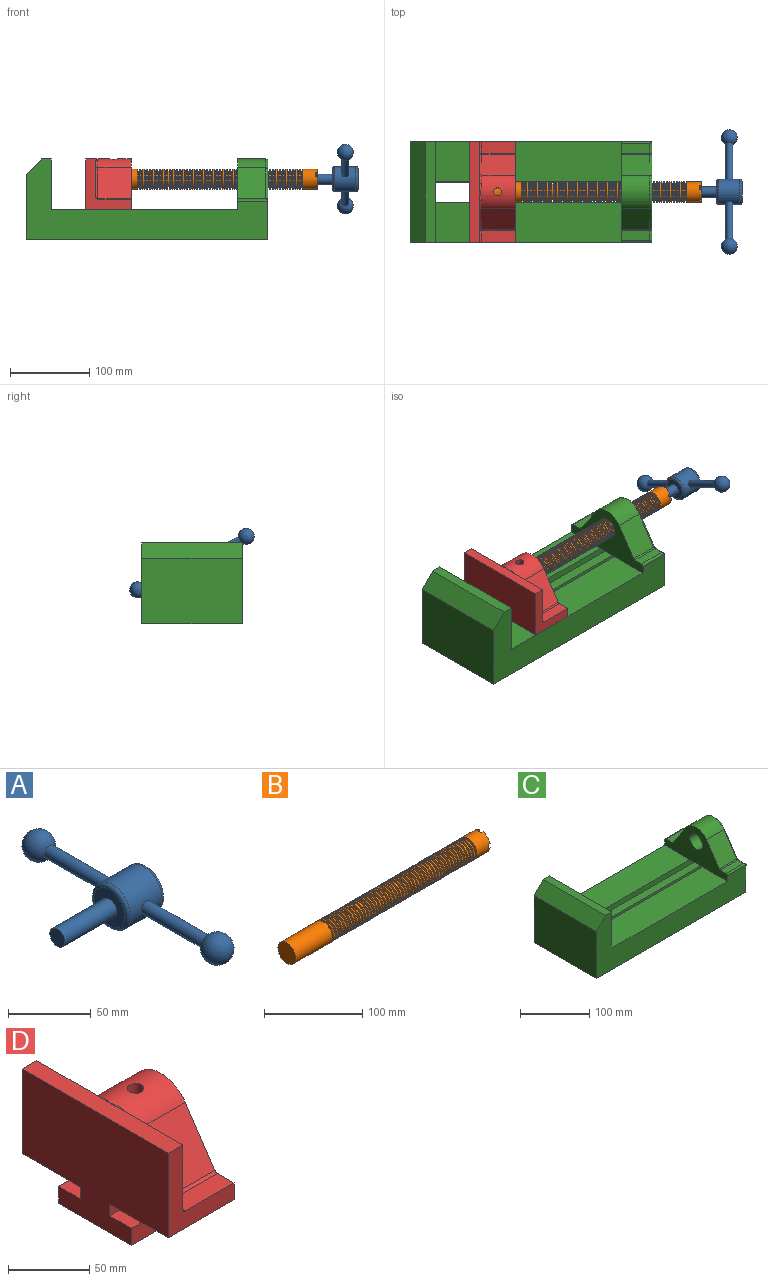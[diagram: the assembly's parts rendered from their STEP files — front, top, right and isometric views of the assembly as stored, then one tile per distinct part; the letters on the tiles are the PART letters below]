
ASSEMBLY  parts=4 mates=3
PART A: 11 faces, bbox 76.2x172.7x34.4 mm
  f0: sphere r=10.16mm, area 1231.8mm2, adj f1
  f1: cylinder r=4.45mm len=51.82mm, axis (0,1,0), area 1438.5mm2, adj f0,f4
  f2: sphere r=10.16mm, area 1231.8mm2, adj f3
  f3: cylinder r=4.45mm len=51.82mm, axis (0,1,0), area 1438.5mm2, adj f2,f4
  f4: cylinder r=15.88mm len=31.75mm, axis (-1,0,0), area 2534.7mm2, adj f1,f3,f9,f10
  f5: cylinder r=6.35mm len=44.45mm, axis (-1,0,0), area 1773.5mm2, adj f6,f8
  f6: plane 12.7x12.7mm, normal (-1,0,0), area 126.7mm2, adj f5
  f7: plane 26.67x26.67mm, normal (1,0,0), area 558.6mm2, adj f10
  f8: plane 26.67x26.67mm, normal (-1,0,0), area 432mm2, adj f5,f9
  f9: torus R=13.33mm, axis (1,0,0), area 374.8mm2, adj f4,f8
  f10: torus R=13.33mm, axis (1,0,0), area 374.8mm2, adj f4,f7
PART B: 220 faces, bbox 279.4x25.4x25.4 mm
  f0: cylinder r=12.7mm len=25.4mm, axis (-1,0,0), area 1468.2mm2, adj f1,f2,f3,f5,f7,f208,f209,f210
  f1: plane 9.9x9.9mm, normal (1,0,0), area 62.3mm2, adj f0,f4,f213,f216
  f2: plane 9.9x9.9mm, normal (1,0,0), area 62.3mm2, adj f0,f4,f210,f218
  f3: plane 9.9x9.9mm, normal (1,0,0), area 62.3mm2, adj f0,f4,f209,f212
  f4: cylinder r=6.35mm len=25.4mm, axis (1,0,0), area 960.3mm2, adj f1,f2,f3,f5,f6,f208,f209,f210
  f5: plane 9.9x9.9mm, normal (1,0,0), area 62.3mm2, adj f0,f4,f215,f217
  f6: plane 12.7x12.7mm, normal (1,0,0), area 126.7mm2, adj f4
  f7: cone r=12.7mm half-angle=76deg, axis (1,0,0), area 188mm2, adj f0,f9
  f8: cone r=10.16mm half-angle=76deg, axis (-1,0,0), area 188mm2, adj f9,f10
  f9: cylinder r=10.16mm len=20.32mm, axis (1,0,0), area 81.1mm2, adj f7,f8
  f10: cylinder r=12.7mm len=25.4mm, axis (-1,0,0), area 131.7mm2, adj f8,f11
  f11: cone r=12.7mm half-angle=76deg, axis (1,0,0), area 188mm2, adj f10,f13
  f12: cone r=10.16mm half-angle=76deg, axis (-1,0,0), area 188mm2, adj f13,f14
  f13: cylinder r=10.16mm len=20.32mm, axis (1,0,0), area 81.1mm2, adj f11,f12
  f14: cylinder r=12.7mm len=25.4mm, axis (-1,0,0), area 131.7mm2, adj f12,f15
  f15: cone r=12.7mm half-angle=76deg, axis (1,0,0), area 188mm2, adj f14,f17
  f16: cone r=10.16mm half-angle=76deg, axis (-1,0,0), area 188mm2, adj f17,f18
  f17: cylinder r=10.16mm len=20.32mm, axis (1,0,0), area 81.1mm2, adj f15,f16
  f18: cylinder r=12.7mm len=25.4mm, axis (-1,0,0), area 131.7mm2, adj f16,f19
  f19: cone r=12.7mm half-angle=76deg, axis (1,0,0), area 188mm2, adj f18,f21
  f20: cone r=10.16mm half-angle=76deg, axis (-1,0,0), area 188mm2, adj f21,f22
  f21: cylinder r=10.16mm len=20.32mm, axis (1,0,0), area 81.1mm2, adj f19,f20
  f22: cylinder r=12.7mm len=25.4mm, axis (-1,0,0), area 131.7mm2, adj f20,f23
  f23: cone r=12.7mm half-angle=76deg, axis (1,0,0), area 188mm2, adj f22,f25
  f24: cone r=10.16mm half-angle=76deg, axis (-1,0,0), area 188mm2, adj f25,f26
  f25: cylinder r=10.16mm len=20.32mm, axis (1,0,0), area 81.1mm2, adj f23,f24
  f26: cylinder r=12.7mm len=25.4mm, axis (-1,0,0), area 131.7mm2, adj f24,f27
  f27: cone r=12.7mm half-angle=76deg, axis (1,0,0), area 188mm2, adj f26,f29
  f28: cone r=10.16mm half-angle=76deg, axis (-1,0,0), area 188mm2, adj f29,f30
  f29: cylinder r=10.16mm len=20.32mm, axis (1,0,0), area 81.1mm2, adj f27,f28
  f30: cylinder r=12.7mm len=25.4mm, axis (-1,0,0), area 131.7mm2, adj f28,f31
  f31: cone r=12.7mm half-angle=76deg, axis (1,0,0), area 188mm2, adj f30,f33
  f32: cone r=10.16mm half-angle=76deg, axis (-1,0,0), area 188mm2, adj f33,f34
  f33: cylinder r=10.16mm len=20.32mm, axis (1,0,0), area 81.1mm2, adj f31,f32
  f34: cylinder r=12.7mm len=25.4mm, axis (-1,0,0), area 131.7mm2, adj f32,f35
  f35: cone r=12.7mm half-angle=76deg, axis (1,0,0), area 188mm2, adj f34,f37
  f36: cone r=10.16mm half-angle=76deg, axis (-1,0,0), area 188mm2, adj f37,f38
  f37: cylinder r=10.16mm len=20.32mm, axis (1,0,0), area 81.1mm2, adj f35,f36
  f38: cylinder r=12.7mm len=25.4mm, axis (-1,0,0), area 131.7mm2, adj f36,f39
  f39: cone r=12.7mm half-angle=76deg, axis (1,0,0), area 188mm2, adj f38,f41
  f40: cone r=10.16mm half-angle=76deg, axis (-1,0,0), area 188mm2, adj f41,f42
  f41: cylinder r=10.16mm len=20.32mm, axis (1,0,0), area 81.1mm2, adj f39,f40
  f42: cylinder r=12.7mm len=25.4mm, axis (-1,0,0), area 131.7mm2, adj f40,f43
  f43: cone r=12.7mm half-angle=76deg, axis (1,0,0), area 188mm2, adj f42,f45
  f44: cone r=10.16mm half-angle=76deg, axis (-1,0,0), area 188mm2, adj f45,f46
  f45: cylinder r=10.16mm len=20.32mm, axis (1,0,0), area 81.1mm2, adj f43,f44
  f46: cylinder r=12.7mm len=25.4mm, axis (-1,0,0), area 131.7mm2, adj f44,f47
  f47: cone r=12.7mm half-angle=76deg, axis (1,0,0), area 188mm2, adj f46,f49
  f48: cone r=10.16mm half-angle=76deg, axis (-1,0,0), area 188mm2, adj f49,f50
  f49: cylinder r=10.16mm len=20.32mm, axis (1,0,0), area 81.1mm2, adj f47,f48
  f50: cylinder r=12.7mm len=25.4mm, axis (-1,0,0), area 131.7mm2, adj f48,f51
  f51: cone r=12.7mm half-angle=76deg, axis (1,0,0), area 188mm2, adj f50,f53
  f52: cone r=10.16mm half-angle=76deg, axis (-1,0,0), area 188mm2, adj f53,f54
  f53: cylinder r=10.16mm len=20.32mm, axis (1,0,0), area 81.1mm2, adj f51,f52
  f54: cylinder r=12.7mm len=25.4mm, axis (-1,0,0), area 131.7mm2, adj f52,f55
  f55: cone r=12.7mm half-angle=76deg, axis (1,0,0), area 188mm2, adj f54,f57
  f56: cone r=10.16mm half-angle=76deg, axis (-1,0,0), area 188mm2, adj f57,f58
  f57: cylinder r=10.16mm len=20.32mm, axis (1,0,0), area 81.1mm2, adj f55,f56
  f58: cylinder r=12.7mm len=25.4mm, axis (-1,0,0), area 131.7mm2, adj f56,f59
  f59: cone r=12.7mm half-angle=76deg, axis (1,0,0), area 188mm2, adj f58,f61
  f60: cone r=10.16mm half-angle=76deg, axis (-1,0,0), area 188mm2, adj f61,f62
  f61: cylinder r=10.16mm len=20.32mm, axis (1,0,0), area 81.1mm2, adj f59,f60
  f62: cylinder r=12.7mm len=25.4mm, axis (-1,0,0), area 131.7mm2, adj f60,f63
  f63: cone r=12.7mm half-angle=76deg, axis (1,0,0), area 188mm2, adj f62,f65
  f64: cone r=10.16mm half-angle=76deg, axis (-1,0,0), area 188mm2, adj f65,f66
  f65: cylinder r=10.16mm len=20.32mm, axis (1,0,0), area 81.1mm2, adj f63,f64
  f66: cylinder r=12.7mm len=25.4mm, axis (-1,0,0), area 131.7mm2, adj f64,f67
  f67: cone r=12.7mm half-angle=76deg, axis (1,0,0), area 188mm2, adj f66,f69
  f68: cone r=10.16mm half-angle=76deg, axis (-1,0,0), area 188mm2, adj f69,f70
  f69: cylinder r=10.16mm len=20.32mm, axis (1,0,0), area 81.1mm2, adj f67,f68
  f70: cylinder r=12.7mm len=25.4mm, axis (-1,0,0), area 131.7mm2, adj f68,f71
  f71: cone r=12.7mm half-angle=76deg, axis (1,0,0), area 188mm2, adj f70,f73
  f72: cone r=10.16mm half-angle=76deg, axis (-1,0,0), area 188mm2, adj f73,f74
  f73: cylinder r=10.16mm len=20.32mm, axis (1,0,0), area 81.1mm2, adj f71,f72
  f74: cylinder r=12.7mm len=25.4mm, axis (-1,0,0), area 131.7mm2, adj f72,f75
  f75: cone r=12.7mm half-angle=76deg, axis (1,0,0), area 188mm2, adj f74,f77
  f76: cone r=10.16mm half-angle=76deg, axis (-1,0,0), area 188mm2, adj f77,f78
  f77: cylinder r=10.16mm len=20.32mm, axis (1,0,0), area 81.1mm2, adj f75,f76
  f78: cylinder r=12.7mm len=25.4mm, axis (-1,0,0), area 131.7mm2, adj f76,f79
  f79: cone r=12.7mm half-angle=76deg, axis (1,0,0), area 188mm2, adj f78,f81
  f80: cone r=10.16mm half-angle=76deg, axis (-1,0,0), area 188mm2, adj f81,f82
  f81: cylinder r=10.16mm len=20.32mm, axis (1,0,0), area 81.1mm2, adj f79,f80
  f82: cylinder r=12.7mm len=25.4mm, axis (-1,0,0), area 131.7mm2, adj f80,f83
  f83: cone r=12.7mm half-angle=76deg, axis (1,0,0), area 188mm2, adj f82,f85
  f84: cone r=10.16mm half-angle=76deg, axis (-1,0,0), area 188mm2, adj f85,f86
  f85: cylinder r=10.16mm len=20.32mm, axis (1,0,0), area 81.1mm2, adj f83,f84
  f86: cylinder r=12.7mm len=25.4mm, axis (-1,0,0), area 131.7mm2, adj f84,f87
  f87: cone r=12.7mm half-angle=76deg, axis (1,0,0), area 188mm2, adj f86,f89
  f88: cone r=10.16mm half-angle=76deg, axis (-1,0,0), area 188mm2, adj f89,f90
  f89: cylinder r=10.16mm len=20.32mm, axis (1,0,0), area 81.1mm2, adj f87,f88
  f90: cylinder r=12.7mm len=25.4mm, axis (-1,0,0), area 131.7mm2, adj f88,f91
  f91: cone r=12.7mm half-angle=76deg, axis (1,0,0), area 188mm2, adj f90,f93
  f92: cone r=10.16mm half-angle=76deg, axis (-1,0,0), area 188mm2, adj f93,f94
  f93: cylinder r=10.16mm len=20.32mm, axis (1,0,0), area 81.1mm2, adj f91,f92
  f94: cylinder r=12.7mm len=25.4mm, axis (-1,0,0), area 131.7mm2, adj f92,f95
  f95: cone r=12.7mm half-angle=76deg, axis (1,0,0), area 188mm2, adj f94,f97
  f96: cone r=10.16mm half-angle=76deg, axis (-1,0,0), area 188mm2, adj f97,f98
  f97: cylinder r=10.16mm len=20.32mm, axis (1,0,0), area 81.1mm2, adj f95,f96
  f98: cylinder r=12.7mm len=25.4mm, axis (-1,0,0), area 131.7mm2, adj f96,f99
  f99: cone r=12.7mm half-angle=76deg, axis (1,0,0), area 188mm2, adj f98,f101
  f100: cone r=10.16mm half-angle=76deg, axis (-1,0,0), area 188mm2, adj f101,f102
  f101: cylinder r=10.16mm len=20.32mm, axis (1,0,0), area 81.1mm2, adj f99,f100
  f102: cylinder r=12.7mm len=25.4mm, axis (-1,0,0), area 131.7mm2, adj f100,f103
  f103: cone r=12.7mm half-angle=76deg, axis (1,0,0), area 188mm2, adj f102,f105
  f104: cone r=10.16mm half-angle=76deg, axis (-1,0,0), area 188mm2, adj f105,f106
  f105: cylinder r=10.16mm len=20.32mm, axis (1,0,0), area 81.1mm2, adj f103,f104
  f106: cylinder r=12.7mm len=25.4mm, axis (-1,0,0), area 131.7mm2, adj f104,f107
  f107: cone r=12.7mm half-angle=76deg, axis (1,0,0), area 188mm2, adj f106,f109
  f108: cone r=10.16mm half-angle=76deg, axis (-1,0,0), area 188mm2, adj f109,f110
  f109: cylinder r=10.16mm len=20.32mm, axis (1,0,0), area 81.1mm2, adj f107,f108
  f110: cylinder r=12.7mm len=25.4mm, axis (-1,0,0), area 131.7mm2, adj f108,f111
  f111: cone r=12.7mm half-angle=76deg, axis (1,0,0), area 188mm2, adj f110,f113
  f112: cone r=10.16mm half-angle=76deg, axis (-1,0,0), area 188mm2, adj f113,f114
  f113: cylinder r=10.16mm len=20.32mm, axis (1,0,0), area 81.1mm2, adj f111,f112
  f114: cylinder r=12.7mm len=25.4mm, axis (-1,0,0), area 131.7mm2, adj f112,f115
  f115: cone r=12.7mm half-angle=76deg, axis (1,0,0), area 188mm2, adj f114,f117
  f116: cone r=10.16mm half-angle=76deg, axis (-1,0,0), area 188mm2, adj f117,f118
  f117: cylinder r=10.16mm len=20.32mm, axis (1,0,0), area 81.1mm2, adj f115,f116
  f118: cylinder r=12.7mm len=25.4mm, axis (-1,0,0), area 131.7mm2, adj f116,f119
  f119: cone r=12.7mm half-angle=76deg, axis (1,0,0), area 188mm2, adj f118,f121
  f120: cone r=10.16mm half-angle=76deg, axis (-1,0,0), area 188mm2, adj f121,f122
  f121: cylinder r=10.16mm len=20.32mm, axis (1,0,0), area 81.1mm2, adj f119,f120
  f122: cylinder r=12.7mm len=25.4mm, axis (-1,0,0), area 131.7mm2, adj f120,f123
  f123: cone r=12.7mm half-angle=76deg, axis (1,0,0), area 188mm2, adj f122,f125
  f124: cone r=10.16mm half-angle=76deg, axis (-1,0,0), area 188mm2, adj f125,f126
  f125: cylinder r=10.16mm len=20.32mm, axis (1,0,0), area 81.1mm2, adj f123,f124
  f126: cylinder r=12.7mm len=25.4mm, axis (-1,0,0), area 131.7mm2, adj f124,f127
  f127: cone r=12.7mm half-angle=76deg, axis (1,0,0), area 188mm2, adj f126,f129
  f128: cone r=10.16mm half-angle=76deg, axis (-1,0,0), area 188mm2, adj f129,f130
  f129: cylinder r=10.16mm len=20.32mm, axis (1,0,0), area 81.1mm2, adj f127,f128
  f130: cylinder r=12.7mm len=25.4mm, axis (-1,0,0), area 131.7mm2, adj f128,f131
  f131: cone r=12.7mm half-angle=76deg, axis (1,0,0), area 188mm2, adj f130,f133
  f132: cone r=10.16mm half-angle=76deg, axis (-1,0,0), area 188mm2, adj f133,f134
  f133: cylinder r=10.16mm len=20.32mm, axis (1,0,0), area 81.1mm2, adj f131,f132
  f134: cylinder r=12.7mm len=25.4mm, axis (-1,0,0), area 131.7mm2, adj f132,f135
  f135: cone r=12.7mm half-angle=76deg, axis (1,0,0), area 188mm2, adj f134,f137
  f136: cone r=10.16mm half-angle=76deg, axis (-1,0,0), area 188mm2, adj f137,f138
  f137: cylinder r=10.16mm len=20.32mm, axis (1,0,0), area 81.1mm2, adj f135,f136
  f138: cylinder r=12.7mm len=25.4mm, axis (-1,0,0), area 131.7mm2, adj f136,f139
  f139: cone r=12.7mm half-angle=76deg, axis (1,0,0), area 188mm2, adj f138,f141
  f140: cone r=10.16mm half-angle=76deg, axis (-1,0,0), area 188mm2, adj f141,f142
  f141: cylinder r=10.16mm len=20.32mm, axis (1,0,0), area 81.1mm2, adj f139,f140
  f142: cylinder r=12.7mm len=25.4mm, axis (-1,0,0), area 131.7mm2, adj f140,f143
  f143: cone r=12.7mm half-angle=76deg, axis (1,0,0), area 188mm2, adj f142,f145
  f144: cone r=10.16mm half-angle=76deg, axis (-1,0,0), area 188mm2, adj f145,f146
  f145: cylinder r=10.16mm len=20.32mm, axis (1,0,0), area 81.1mm2, adj f143,f144
  f146: cylinder r=12.7mm len=25.4mm, axis (-1,0,0), area 131.7mm2, adj f144,f147
  f147: cone r=12.7mm half-angle=76deg, axis (1,0,0), area 188mm2, adj f146,f149
  f148: cone r=10.16mm half-angle=76deg, axis (-1,0,0), area 188mm2, adj f149,f150
  f149: cylinder r=10.16mm len=20.32mm, axis (1,0,0), area 81.1mm2, adj f147,f148
  f150: cylinder r=12.7mm len=25.4mm, axis (-1,0,0), area 131.7mm2, adj f148,f151
  f151: cone r=12.7mm half-angle=76deg, axis (1,0,0), area 188mm2, adj f150,f153
  f152: cone r=10.16mm half-angle=76deg, axis (-1,0,0), area 188mm2, adj f153,f154
  f153: cylinder r=10.16mm len=20.32mm, axis (1,0,0), area 81.1mm2, adj f151,f152
  f154: cylinder r=12.7mm len=25.4mm, axis (-1,0,0), area 131.7mm2, adj f152,f155
  f155: cone r=12.7mm half-angle=76deg, axis (1,0,0), area 188mm2, adj f154,f157
  f156: cone r=10.16mm half-angle=76deg, axis (-1,0,0), area 188mm2, adj f157,f158
  f157: cylinder r=10.16mm len=20.32mm, axis (1,0,0), area 81.1mm2, adj f155,f156
  f158: cylinder r=12.7mm len=25.4mm, axis (-1,0,0), area 131.7mm2, adj f156,f159
  f159: cone r=12.7mm half-angle=76deg, axis (1,0,0), area 188mm2, adj f158,f161
  f160: cone r=10.16mm half-angle=76deg, axis (-1,0,0), area 188mm2, adj f161,f162
  f161: cylinder r=10.16mm len=20.32mm, axis (1,0,0), area 81.1mm2, adj f159,f160
  f162: cylinder r=12.7mm len=25.4mm, axis (-1,0,0), area 131.7mm2, adj f160,f163
  f163: cone r=12.7mm half-angle=76deg, axis (1,0,0), area 188mm2, adj f162,f165
  f164: cone r=10.16mm half-angle=76deg, axis (-1,0,0), area 188mm2, adj f165,f166
  f165: cylinder r=10.16mm len=20.32mm, axis (1,0,0), area 81.1mm2, adj f163,f164
  f166: cylinder r=12.7mm len=25.4mm, axis (-1,0,0), area 131.7mm2, adj f164,f167
  f167: cone r=12.7mm half-angle=76deg, axis (1,0,0), area 188mm2, adj f166,f169
  f168: cone r=10.16mm half-angle=76deg, axis (-1,0,0), area 188mm2, adj f169,f170
  f169: cylinder r=10.16mm len=20.32mm, axis (1,0,0), area 81.1mm2, adj f167,f168
  f170: cylinder r=12.7mm len=25.4mm, axis (-1,0,0), area 131.7mm2, adj f168,f171
  f171: cone r=12.7mm half-angle=76deg, axis (1,0,0), area 188mm2, adj f170,f173
  f172: cone r=10.16mm half-angle=76deg, axis (-1,0,0), area 188mm2, adj f173,f174
  f173: cylinder r=10.16mm len=20.32mm, axis (1,0,0), area 81.1mm2, adj f171,f172
  f174: cylinder r=12.7mm len=25.4mm, axis (-1,0,0), area 131.7mm2, adj f172,f175
  f175: cone r=12.7mm half-angle=76deg, axis (1,0,0), area 188mm2, adj f174,f177
  f176: cone r=10.16mm half-angle=76deg, axis (-1,0,0), area 188mm2, adj f177,f178
  f177: cylinder r=10.16mm len=20.32mm, axis (1,0,0), area 81.1mm2, adj f175,f176
  f178: cylinder r=12.7mm len=25.4mm, axis (-1,0,0), area 131.7mm2, adj f176,f179
  f179: cone r=12.7mm half-angle=76deg, axis (1,0,0), area 188mm2, adj f178,f181
  f180: cone r=10.16mm half-angle=76deg, axis (-1,0,0), area 188mm2, adj f181,f182
  f181: cylinder r=10.16mm len=20.32mm, axis (1,0,0), area 81.1mm2, adj f179,f180
  f182: cylinder r=12.7mm len=25.4mm, axis (-1,0,0), area 131.7mm2, adj f180,f183
  f183: cone r=12.7mm half-angle=76deg, axis (1,0,0), area 188mm2, adj f182,f185
  f184: cone r=10.16mm half-angle=76deg, axis (-1,0,0), area 188mm2, adj f185,f186
  f185: cylinder r=10.16mm len=20.32mm, axis (1,0,0), area 81.1mm2, adj f183,f184
  f186: cylinder r=12.7mm len=25.4mm, axis (-1,0,0), area 131.7mm2, adj f184,f187
  f187: cone r=12.7mm half-angle=76deg, axis (1,0,0), area 188mm2, adj f186,f189
  f188: cone r=10.16mm half-angle=76deg, axis (-1,0,0), area 188mm2, adj f189,f190
  f189: cylinder r=10.16mm len=20.32mm, axis (1,0,0), area 81.1mm2, adj f187,f188
  f190: cylinder r=12.7mm len=25.4mm, axis (-1,0,0), area 131.7mm2, adj f188,f191
  f191: cone r=12.7mm half-angle=76deg, axis (1,0,0), area 188mm2, adj f190,f193
  f192: cone r=10.16mm half-angle=76deg, axis (-1,0,0), area 188mm2, adj f193,f194
  f193: cylinder r=10.16mm len=20.32mm, axis (1,0,0), area 81.1mm2, adj f191,f192
  f194: cylinder r=12.7mm len=25.4mm, axis (-1,0,0), area 131.7mm2, adj f192,f195
  f195: cone r=12.7mm half-angle=76deg, axis (1,0,0), area 188mm2, adj f194,f197
  f196: cone r=10.16mm half-angle=76deg, axis (-1,0,0), area 188mm2, adj f197,f198
  f197: cylinder r=10.16mm len=20.32mm, axis (1,0,0), area 81.1mm2, adj f195,f196
  f198: cylinder r=12.7mm len=25.4mm, axis (-1,0,0), area 131.7mm2, adj f196,f199
  f199: cone r=12.7mm half-angle=76deg, axis (1,0,0), area 188mm2, adj f198,f201
  f200: cone r=10.16mm half-angle=76deg, axis (-1,0,0), area 188mm2, adj f201,f202
  f201: cylinder r=10.16mm len=20.32mm, axis (1,0,0), area 81.1mm2, adj f199,f200
  f202: cylinder r=12.7mm len=25.4mm, axis (-1,0,0), area 131.7mm2, adj f200,f203
  f203: cone r=12.7mm half-angle=76deg, axis (1,0,0), area 188mm2, adj f202,f205
  f204: cone r=10.16mm half-angle=76deg, axis (-1,0,0), area 188mm2, adj f205,f207
  f205: cylinder r=10.16mm len=20.32mm, axis (1,0,0), area 81.1mm2, adj f203,f204
  f206: plane 25.4x25.4mm, normal (-1,0,0), area 506.7mm2, adj f207
  f207: cylinder r=12.7mm len=52.45mm, axis (-1,0,0), area 4185.4mm2, adj f204,f206
  f208: plane 6.88x5.08mm, normal (1,0,0), area 32.7mm2, adj f0,f4,f209,f210
  f209: plane 6.62x2.54mm, normal (0,-1,0), area 16.8mm2, adj f0,f3,f4,f208
  f210: plane 6.62x2.54mm, normal (0,1,0), area 16.8mm2, adj f0,f2,f4,f208
  f211: plane 6.88x5.08mm, normal (1,0,0), area 32.7mm2, adj f0,f4,f212,f213
  f212: plane 6.62x2.54mm, normal (0,0,1), area 16.8mm2, adj f0,f3,f4,f211
  f213: plane 6.62x2.54mm, normal (0,0,-1), area 16.8mm2, adj f0,f1,f4,f211
  f214: plane 6.88x5.08mm, normal (1,0,0), area 32.7mm2, adj f0,f4,f215,f216
  f215: plane 6.62x2.54mm, normal (0,1,0), area 16.8mm2, adj f0,f4,f5,f214
  f216: plane 6.62x2.54mm, normal (0,-1,0), area 16.8mm2, adj f0,f1,f4,f214
  f217: plane 6.62x2.54mm, normal (0,0,-1), area 16.8mm2, adj f0,f4,f5,f219
  f218: plane 6.62x2.54mm, normal (0,0,1), area 16.8mm2, adj f0,f2,f4,f219
  f219: plane 6.88x5.08mm, normal (1,0,0), area 32.7mm2, adj f0,f4,f217,f218
PART C: 39 faces, bbox 304.8x127x103.7 mm
  f0: plane 234.95x50.8mm, normal (0,0,1), area 11935.5mm2, adj f3,f8,f16,f26
  f1: plane 127x99.06mm, normal (1,0,0), area 7097.5mm2, adj f7,f8,f9,f14,f17,f18,f19,f20
  f2: plane 234.95x50.8mm, normal (0,0,1), area 11935.5mm2, adj f3,f9,f16,f27
  f3: plane 127x101.6mm, normal (1,0,0), area 9516.1mm2, adj f0,f2,f4,f7,f8,f9,f18,f19
  f4: plane 127x12.7mm, normal (0,0,1), area 1612.9mm2, adj f3,f5,f8,f9
  f5: plane 127x19.05mm, normal (-0.71,0,0.71), area 3421.5mm2, adj f4,f6,f8,f9
  f6: plane 127x82.55mm, normal (-1,0,0), area 10483.8mm2, adj f5,f7,f8,f9
  f7: plane 304.8x127mm, normal (0,0,-1), area 31774.1mm2, adj f1,f3,f6,f8,f9,f21,f22
  f8: plane 304.8x101.6mm, normal (0,-1,0), area 13834.6mm2, adj f0,f1,f3,f4,f5,f6,f7,f16
  f9: plane 304.8x101.6mm, normal (0,1,0), area 13834.6mm2, adj f1,f2,f3,f4,f5,f6,f7,f16
  f10: plane 35.56x11.98mm, normal (0,0,1), area 426mm2, adj f16,f28,f29,f30
  f11: plane 38.43x35.56mm, normal (0,0.83,0.56), area 1645.4mm2, adj f12,f16,f29,f32
  f12: cylinder r=25.4mm len=42.19mm, axis (1,0,0), area 1770.2mm2, adj f11,f13,f16,f33
  f13: plane 38.43x35.56mm, normal (0,-0.83,0.56), area 1645.4mm2, adj f12,f16,f34,f35
  f14: cylinder r=12.7mm len=38.1mm, axis (1,0,0), area 3040.2mm2, adj f1,f16
  f15: plane 35.56x11.98mm, normal (0,0,1), area 426mm2, adj f16,f34,f36,f38
  f16: plane 127x63.5mm, normal (-1,0,0), area 4155.5mm2, adj f0,f2,f8,f9,f10,f11,f12,f13
  f17: plane 38.1x25.4mm, normal (0,0,-1), area 967.7mm2, adj f1,f16,f26,f27
  f18: plane 273.05x19.05mm, normal (0,0,-1), area 5201.6mm2, adj f1,f3,f19,f26
  f19: plane 273.05x12.7mm, normal (0,1,0), area 3467.7mm2, adj f1,f3,f18,f20
  f20: plane 273.05x19.05mm, normal (0,0,1), area 5201.6mm2, adj f1,f3,f19,f21
  f21: plane 273.05x16.51mm, normal (0,1,0), area 4508.1mm2, adj f1,f3,f7,f20
  f22: plane 273.05x16.51mm, normal (0,-1,0), area 4508.1mm2, adj f1,f3,f7,f23
  f23: plane 273.05x19.05mm, normal (0,0,1), area 5201.6mm2, adj f1,f3,f22,f24
  f24: plane 273.05x12.7mm, normal (0,-1,0), area 3467.7mm2, adj f1,f3,f23,f25
  f25: plane 273.05x19.05mm, normal (0,0,-1), area 5201.6mm2, adj f1,f3,f24,f27
  f26: plane 273.05x8.89mm, normal (0,1,0), area 2427.4mm2, adj f0,f1,f3,f17,f18
  f27: plane 273.05x8.89mm, normal (0,-1,0), area 2427.4mm2, adj f1,f2,f3,f17,f25
  f28: cylinder r=2.54mm len=38.1mm, axis (1,0,0), area 148.3mm2, adj f9,f10,f16,f30
  f29: cylinder r=2.54mm len=35.56mm, axis (-1,0,0), area 88.5mm2, adj f10,f11,f16,f31
  f30: cylinder r=2.54mm len=14.52mm, axis (0,1,0), area 54.3mm2, adj f1,f10,f28,f31
  f31: torus R=5.08mm, axis (-1,0,0), area 13.5mm2, adj f1,f29,f30,f32
  f32: cylinder r=2.54mm len=39.84mm, axis (0,0.56,-0.83), area 184.6mm2, adj f1,f11,f31,f33
  f33: torus R=22.86mm, axis (-1,0,0), area 191.4mm2, adj f1,f12,f32,f35
  f34: cylinder r=2.54mm len=35.56mm, axis (-1,0,0), area 88.5mm2, adj f13,f15,f16,f37
  f35: cylinder r=2.54mm len=39.84mm, axis (0,0.56,0.83), area 184.6mm2, adj f1,f13,f33,f37
  f36: cylinder r=2.54mm len=38.1mm, axis (-1,0,0), area 148.3mm2, adj f8,f15,f16,f38
  f37: torus R=5.08mm, axis (-1,0,0), area 13.5mm2, adj f1,f34,f35,f38
  f38: cylinder r=2.54mm len=14.52mm, axis (0,1,0), area 54.3mm2, adj f1,f15,f36,f37
PART D: 36 faces, bbox 57.2x127x89 mm
  f0: plane 57.15x50.8mm, normal (0,0,-1), area 2903.2mm2, adj f6,f9,f10,f23
  f1: cylinder r=12.7mm len=44.45mm, axis (1,0,0), area 3464.3mm2, adj f6,f15,f16
  f2: plane 41.91x14.52mm, normal (0,0,1), area 608.5mm2, adj f6,f11,f24,f25
  f3: plane 51.86x48.26mm, normal (1,0,0), area 1495.7mm2, adj f8,f10,f31,f33,f35
  f4: plane 51.86x48.26mm, normal (1,0,0), area 1495.7mm2, adj f8,f11,f24,f28,f29
  f5: plane 57.15x50.8mm, normal (0,0,-1), area 2903.2mm2, adj f6,f9,f11,f22
  f6: plane 127x85.09mm, normal (1,0,0), area 5190.6mm2, adj f0,f1,f2,f5,f7,f10,f11,f12
  f7: plane 41.91x14.52mm, normal (0,0,1), area 608.5mm2, adj f6,f10,f30,f31
  f8: plane 127x12.7mm, normal (0,0,1), area 1612.9mm2, adj f3,f4,f9,f10,f11,f26,f34
  f9: plane 127x85.09mm, normal (-1,0,0), area 9096.8mm2, adj f0,f5,f8,f10,f11,f17,f18,f19
  f10: plane 63.5x57.15mm, normal (0,-1,0), area 1372.3mm2, adj f0,f3,f6,f7,f8,f9,f31
  f11: plane 63.5x57.15mm, normal (0,1,0), area 1372.3mm2, adj f2,f4,f5,f6,f8,f9,f24
  f12: plane 41.91x38.43mm, normal (0,-0.83,0.56), area 1939.2mm2, adj f6,f13,f30,f33
  f13: cylinder r=25.4mm len=44.45mm, axis (1,0,0), area 2026.5mm2, adj f6,f12,f14,f16,f26,f28,f34,f35
  f14: plane 41.91x38.43mm, normal (0,0.83,0.56), area 1939.2mm2, adj f6,f13,f25,f29
  f15: plane 25.4x25.4mm, normal (1,0,0), area 506.7mm2, adj f1
  f16: cylinder r=5.08mm len=13.76mm, axis (0,0,1), area 414mm2, adj f1,f13
  f17: plane 57.15x19.05mm, normal (0,0,1), area 1088.7mm2, adj f6,f9,f18,f23
  f18: plane 57.15x12.7mm, normal (0,-1,0), area 725.8mm2, adj f6,f9,f17,f19
  f19: plane 63.5x57.15mm, normal (0,0,-1), area 3629mm2, adj f6,f9,f18,f20
  f20: plane 57.15x12.7mm, normal (0,1,0), area 725.8mm2, adj f6,f9,f19,f21
  f21: plane 57.15x19.05mm, normal (0,0,1), area 1088.7mm2, adj f6,f9,f20,f22
  f22: plane 57.15x8.89mm, normal (0,1,0), area 508.1mm2, adj f5,f6,f9,f21
  f23: plane 57.15x8.89mm, normal (0,-1,0), area 508.1mm2, adj f0,f6,f9,f17
  f24: cylinder r=2.54mm len=14.52mm, axis (0,-1,0), area 57.9mm2, adj f2,f4,f11,f27
  f25: cylinder r=2.54mm len=41.91mm, axis (1,0,0), area 104.3mm2, adj f2,f6,f14,f27
  f26: bspline ~12.24x2.8mm, area 20.9mm2, adj f8,f13,f28
  f27: sphere r=2.54mm, area 6.3mm2, adj f24,f25,f29
  f28: torus R=27.94mm, axis (1,0,0), area 57.8mm2, adj f4,f13,f26,f29
  f29: cylinder r=2.54mm len=39.84mm, axis (0,-0.56,0.83), area 184.6mm2, adj f4,f14,f27,f28
  f30: cylinder r=2.54mm len=41.91mm, axis (1,0,0), area 104.3mm2, adj f6,f7,f12,f32
  f31: cylinder r=2.54mm len=14.52mm, axis (0,-1,0), area 57.9mm2, adj f3,f7,f10,f32
  f32: sphere r=2.54mm, area 6.3mm2, adj f30,f31,f33
  f33: cylinder r=2.54mm len=39.84mm, axis (0,-0.56,-0.83), area 184.6mm2, adj f3,f12,f32,f35
  f34: bspline ~12.24x2.8mm, area 20.9mm2, adj f8,f13,f35
  f35: torus R=27.94mm, axis (1,0,0), area 57.8mm2, adj f3,f13,f33,f34
PLACE A rot(axis=(1,0,0),153.8deg) t=(49.74,32.11,111.77)mm
PLACE B rot(axis=(1,0,0),153.8deg) t=(49.74,32.11,111.77)mm
PLACE C t=(6.09,-1.57,-32.78)mm fixed
PLACE D t=(49.74,-1.57,-32.78)mm
MATE revolute D.f28 <-> B.f7  axis (1,0,0) through (-210.61,-1.57,43.42)mm
MATE slider D.f9 <-> C.f3  axis (-1,0,0) through (-223.31,-65.07,5.32)mm
MATE fastened A.f5 <-> B.f4  axis (-1,0,0) through (43.39,-1.57,43.42)mm
